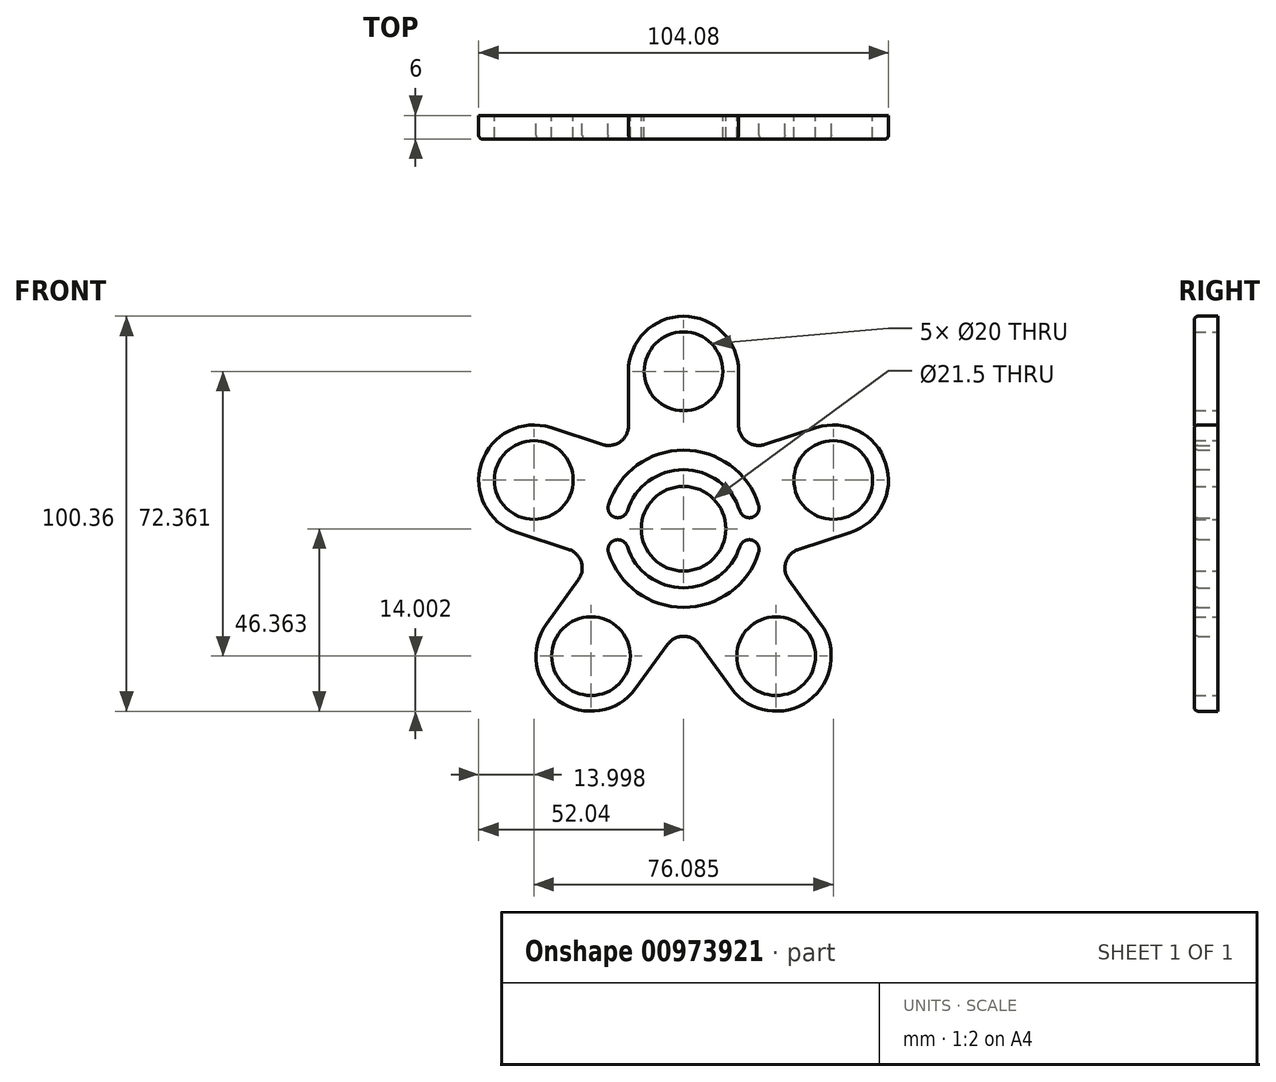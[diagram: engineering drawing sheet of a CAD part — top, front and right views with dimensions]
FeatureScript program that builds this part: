
annotation { "Feature Type Name" : "Feature", "Feature Type Description" : "" }
export const myFeature = defineFeature(function(context is Context, id is Id, definition is map)
    precondition{}
    {
        {
            var Q0;
            Q0=qCreatedBy(makeId("Front.planeOp"),FACE);
            var sketch = newSketch(context, id + "F0", { "sketchPlane" : qUnion([Q0])});
            skCircle(sketch, "E0", {"center": v(0, 1.45) * mm, "radius": 10.75 * mm});
            skLineSegment(sketch, "E1", {"start": v(0, 1.45) * mm, "end": v(0, 41.45) * mm, "construction": true});
            skCircle(sketch, "E2", {"center": v(0, 41.45) * mm, "radius": 10 * mm});
            skCircle(sketch, "E3.1.0", {"center": v(-38.04, 13.81) * mm, "radius": 10 * mm});
            skCircle(sketch, "E3.2.0", {"center": v(-23.51, -30.9) * mm, "radius": 10 * mm});
            skCircle(sketch, "E3.3.0", {"center": v(23.51, -30.9) * mm, "radius": 10 * mm});
            skCircle(sketch, "E3.4.0", {"center": v(38.04, 13.81) * mm, "radius": 10 * mm});
            skLineSegment(sketch, "E4.left", {"start": v(14, 41.45) * mm, "end": v(14, 27.6) * mm});
            skLineSegment(sketch, "E4.right", {"start": v(-14, 41.45) * mm, "end": v(-14, 27.6) * mm});
            skArc(sketch, "E5", {"start": v(14, 41.45) * mm, "mid": v(0, 55.45) * mm, "end": v(-14, 41.45) * mm});
            skLineSegment(sketch, "E6.1.0", {"start": v(-33.72, 27.13) * mm, "end": v(-20.55, 22.85) * mm});
            skArc(sketch, "E6.1.1", {"start": v(-33.72, 27.13) * mm, "mid": v(-51.36, 18.14) * mm, "end": v(-42.37, 0.5) * mm});
            skLineSegment(sketch, "E6.1.2", {"start": v(-42.37, 0.5) * mm, "end": v(-29.2, -3.78) * mm});
            skLineSegment(sketch, "E6.2.0", {"start": v(-34.84, -22.68) * mm, "end": v(-26.7, -11.47) * mm});
            skArc(sketch, "E6.2.1", {"start": v(-34.84, -22.68) * mm, "mid": v(-31.74, -42.23) * mm, "end": v(-12.19, -39.14) * mm});
            skLineSegment(sketch, "E6.2.2", {"start": v(-12.19, -39.14) * mm, "end": v(-4.05, -27.93) * mm});
            skLineSegment(sketch, "E6.3.0", {"start": v(12.19, -39.14) * mm, "end": v(4.05, -27.93) * mm});
            skArc(sketch, "E6.3.1", {"start": v(12.19, -39.14) * mm, "mid": v(31.74, -42.23) * mm, "end": v(34.84, -22.68) * mm});
            skLineSegment(sketch, "E6.3.2", {"start": v(34.84, -22.68) * mm, "end": v(26.7, -11.47) * mm});
            skLineSegment(sketch, "E6.4.0", {"start": v(42.37, 0.5) * mm, "end": v(29.2, -3.78) * mm});
            skArc(sketch, "E6.4.1", {"start": v(42.37, 0.5) * mm, "mid": v(51.36, 18.14) * mm, "end": v(33.72, 27.13) * mm});
            skLineSegment(sketch, "E6.4.2", {"start": v(33.72, 27.13) * mm, "end": v(20.55, 22.85) * mm});
            skPoint(sketch, "E7.orphan", {"position": v(-17.5, 1.19) * mm});
            skPoint(sketch, "E8.orphan", {"position": v(-14.31, -8.62) * mm});
            skPoint(sketch, "E9.orphan", {"position": v(-5.15, -15.27) * mm});
            skPoint(sketch, "E10.orphan", {"position": v(5.15, -15.27) * mm});
            skPoint(sketch, "E11.orphan", {"position": v(14.31, -8.62) * mm});
            skPoint(sketch, "E12.orphan", {"position": v(17.5, 1.19) * mm});
            skArc(sketch, "E13.filletArc", {"start": v(-20.55, 22.85) * mm, "mid": v(-16.06, 23.56) * mm, "end": v(-14, 27.6) * mm});
            skArc(sketch, "E14.filletArc", {"start": v(14, 27.6) * mm, "mid": v(16.06, 23.56) * mm, "end": v(20.55, 22.85) * mm});
            skPoint(sketch, "E15.visualSharp", {"position": v(22.65, -5.9) * mm});
            skArc(sketch, "E15.filletArc", {"start": v(29.2, -3.78) * mm, "mid": v(25.99, -7) * mm, "end": v(26.7, -11.47) * mm});
            skPoint(sketch, "E16.visualSharp", {"position": v(0, -22.37) * mm});
            skArc(sketch, "E16.filletArc", {"start": v(4.05, -27.93) * mm, "mid": v(0, -25.87) * mm, "end": v(-4.05, -27.93) * mm});
            skPoint(sketch, "E17.visualSharp", {"position": v(-22.65, -5.9) * mm});
            skArc(sketch, "E17.filletArc", {"start": v(-26.7, -11.47) * mm, "mid": v(-25.99, -7) * mm, "end": v(-29.2, -3.78) * mm});
            skArc(sketch, "E18", {"start": v(-16.68, -3.84) * mm, "mid": v(0, -16.05) * mm, "end": v(16.68, -3.84) * mm});
            skArc(sketch, "E19.trimOffspring", {"start": v(16.68, 6.74) * mm, "mid": v(0, 18.95) * mm, "end": v(-16.68, 6.74) * mm});
            skArc(sketch, "E20.0.startCap", {"start": v(19.06, 7.5) * mm, "mid": v(17.44, 4.36) * mm, "end": v(14.3, 5.99) * mm});
            skArc(sketch, "E20.0.endCap", {"start": v(-14.3, 5.99) * mm, "mid": v(-17.44, 4.36) * mm, "end": v(-19.06, 7.5) * mm});
            skArc(sketch, "E20.0.left", {"start": v(14.3, 5.99) * mm, "mid": v(0, 16.45) * mm, "end": v(-14.3, 5.99) * mm});
            skArc(sketch, "E20.0.right", {"start": v(19.06, 7.5) * mm, "mid": v(0, 21.45) * mm, "end": v(-19.06, 7.5) * mm});
            skArc(sketch, "E21.0.startCap", {"start": v(-19.06, -4.6) * mm, "mid": v(-17.44, -1.45) * mm, "end": v(-14.3, -3.08) * mm});
            skArc(sketch, "E21.0.endCap", {"start": v(14.3, -3.08) * mm, "mid": v(17.44, -1.45) * mm, "end": v(19.06, -4.6) * mm});
            skArc(sketch, "E21.0.left", {"start": v(-14.3, -3.08) * mm, "mid": v(0, -13.55) * mm, "end": v(14.3, -3.08) * mm});
            skArc(sketch, "E21.0.right", {"start": v(-19.06, -4.6) * mm, "mid": v(0, -18.55) * mm, "end": v(19.06, -4.6) * mm});
            skSolve(sketch);
        }
        {
            var Q0;
            Q0=makeQuery(id+"F0.imprint","IMPRINT",FACE,{"disambiguationData":[TD([[makeQuery(id+"F0.imprint","IMPRINT",EDGE,{"derivedFrom":sQuery(id+"F0.wireOp",EDGE,"E0")}),-1.0]])]});
            extrude(context, id + "F1", {"entities" : qUnion([Q0]), "depth" : 6 * mm, "offsetDistance" : 25 * mm});
        }
        {
            var Q0;
            Q0=makeQuery(id+"F1.opExtrude","CAP_EDGE",EDGE,{"disambiguationData":[OSD([sQuery(id+"F0.wireOp",EDGE,"E4.right")])],"isStart":false});
            var Q1;
            Q1=makeQuery(id+"F1.opExtrude","CAP_EDGE",EDGE,{"disambiguationData":[OSD([sQuery(id+"F0.wireOp",EDGE,"E5")])],"isStart":false});
            var Q2;
            Q2=makeQuery(id+"F1.opExtrude","CAP_EDGE",EDGE,{"disambiguationData":[OSD([sQuery(id+"F0.wireOp",EDGE,"E4.left")])],"isStart":false});
            var Q3;
            Q3=makeQuery(id+"F1.opExtrude","CAP_EDGE",EDGE,{"disambiguationData":[OSD([sQuery(id+"F0.wireOp",EDGE,"E21.0.right")])],"isStart":false});
            var Q4;
            Q4=makeQuery(id+"F1.opExtrude","CAP_EDGE",EDGE,{"disambiguationData":[OSD([sQuery(id+"F0.wireOp",EDGE,"E20.0.right")])],"isStart":false});
            fillet(context, id + "F2", {"entities" : qUnion([Q0, Q1, Q2, Q3, Q4]), "radius" : 1 * mm, "tangentPropagation" : true, "allowEdgeOverflow" : false});
        }
    });
